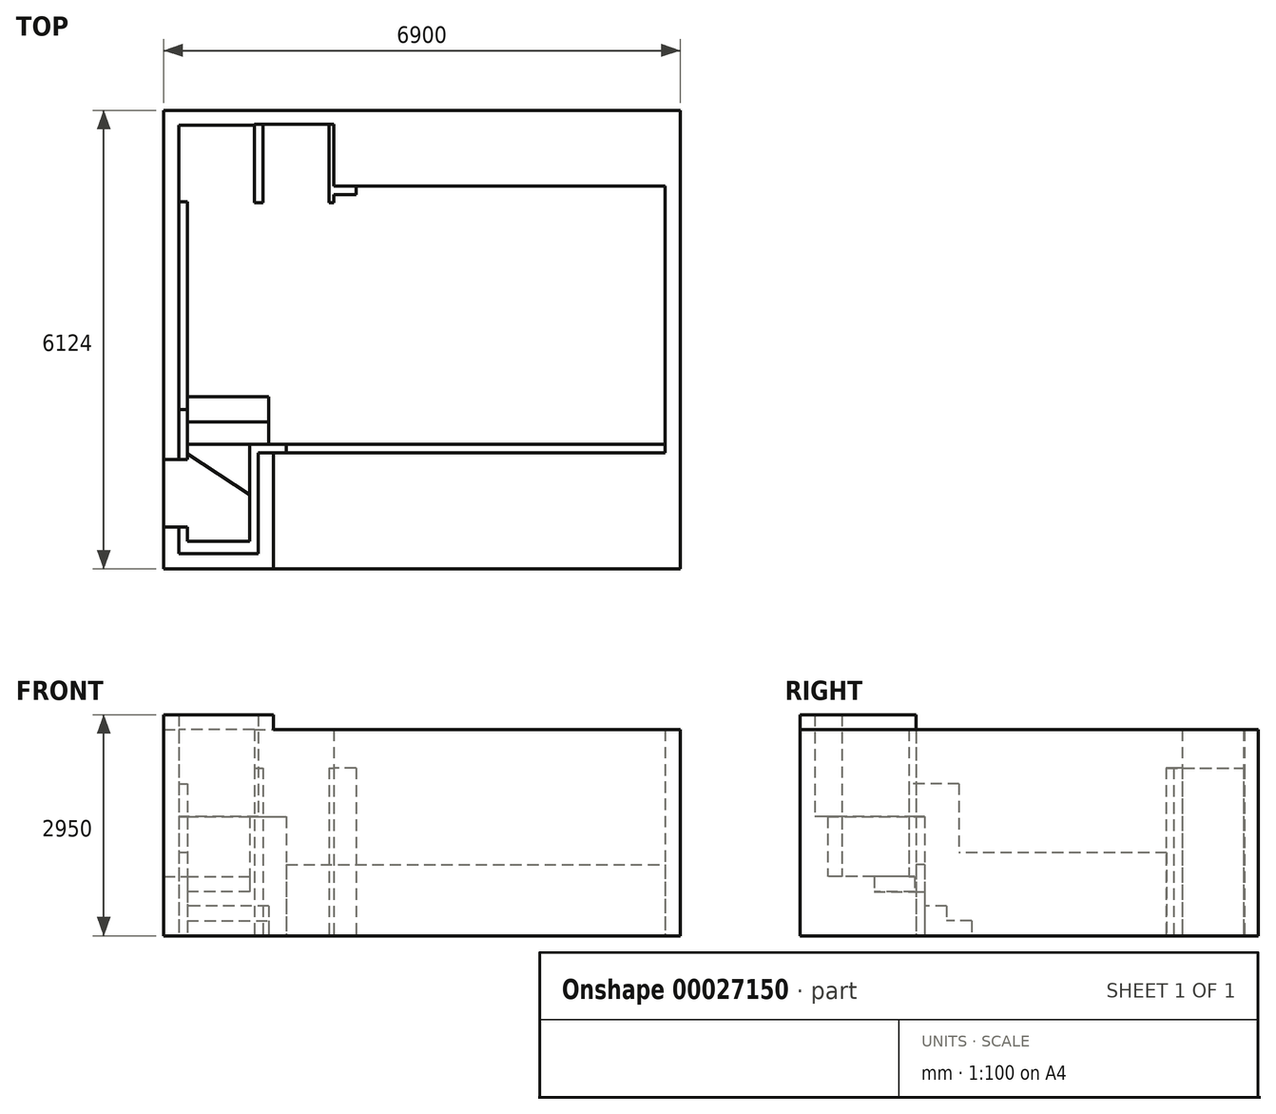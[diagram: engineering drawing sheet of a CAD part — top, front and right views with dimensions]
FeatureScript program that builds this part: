
annotation { "Feature Type Name" : "Feature", "Feature Type Description" : "" }
export const myFeature = defineFeature(function(context is Context, id is Id, definition is map)
    precondition{}
    {
        {
            var Q0;
            Q0=qCreatedBy(makeId("Top.planeOp"),FACE);
            var sketch = newSketch(context, id + "F0", { "sketchPlane" : qUnion([Q0])});
            skLineSegment(sketch, "E0", {"start": v(0, 0) * mm, "end": v(5550, 0) * mm});
            skLineSegment(sketch, "E1", {"start": v(5550, 0) * mm, "end": v(5550, 3560) * mm});
            skLineSegment(sketch, "E2", {"start": v(5550, 3560) * mm, "end": v(1060, 3560) * mm});
            skLineSegment(sketch, "E3", {"start": v(1060, 3342) * mm, "end": v(1060, 3560) * mm});
            skLineSegment(sketch, "E4", {"start": v(1060, 3342) * mm, "end": v(60, 3342) * mm});
            skLineSegment(sketch, "E5", {"start": v(0, 0) * mm, "end": v(0, -1350) * mm});
            skLineSegment(sketch, "E6", {"start": v(60, 3342) * mm, "end": v(60, 4374) * mm});
            skLineSegment(sketch, "E7", {"start": v(60, 4374) * mm, "end": v(-950, 4374) * mm});
            skLineSegment(sketch, "E8", {"start": v(-950, 4374) * mm, "end": v(-950, 3349) * mm});
            skLineSegment(sketch, "E9", {"start": v(-950, 3349) * mm, "end": v(-950, -91) * mm});
            skLineSegment(sketch, "E10", {"start": v(0, 115) * mm, "end": v(490, 115) * mm});
            skLineSegment(sketch, "E11", {"start": v(490, 115) * mm, "end": v(5550, 115) * mm});
            skLineSegment(sketch, "E12", {"start": v(0, 0) * mm, "end": v(0, 115) * mm});
            skLineSegment(sketch, "E13", {"start": v(5435, 0) * mm, "end": v(5435, 3560) * mm});
            skLineSegment(sketch, "E14", {"start": v(5435, 115) * mm, "end": v(5550, 115) * mm});
            skLineSegment(sketch, "E15", {"start": v(1060, 3445) * mm, "end": v(5550, 3445) * mm});
            skLineSegment(sketch, "E16", {"start": v(5435, 3445) * mm, "end": v(5435, 3560) * mm});
            skPoint(sketch, "E17", {"position": v(1420, 3560) * mm});
            skPoint(sketch, "E18", {"position": v(1120, 3560) * mm});
            skLineSegment(sketch, "E19", {"start": v(1120, 3560) * mm, "end": v(1120, 3342) * mm});
            skLineSegment(sketch, "E20", {"start": v(1120, 3342) * mm, "end": v(1060, 3342) * mm});
            skLineSegment(sketch, "E21", {"start": v(1420, 3560) * mm, "end": v(1420, 3445) * mm});
            skLineSegment(sketch, "E22", {"start": v(175, 3342) * mm, "end": v(175, 4374) * mm});
            skLineSegment(sketch, "E23", {"start": v(175, 4374) * mm, "end": v(60, 4374) * mm});
            skLineSegment(sketch, "E24", {"start": v(-950, -91) * mm, "end": v(-835, -91) * mm});
            skLineSegment(sketch, "E25", {"start": v(-835, -91) * mm, "end": v(-835, 3349) * mm});
            skLineSegment(sketch, "E26", {"start": v(-835, 3349) * mm, "end": v(-950, 3349) * mm});
            skLineSegment(sketch, "E27", {"start": v(-835, 745) * mm, "end": v(255, 745) * mm});
            skLineSegment(sketch, "E28", {"start": v(255, 745) * mm, "end": v(255, 115) * mm});
            skLineSegment(sketch, "E29", {"start": v(-835, 410) * mm, "end": v(255, 410) * mm});
            skLineSegment(sketch, "E30", {"start": v(0, 115) * mm, "end": v(-835, 115) * mm});
            skPoint(sketch, "E31", {"position": v(-835, -15) * mm});
            skPoint(sketch, "E32", {"position": v(0, -560) * mm});
            skLineSegment(sketch, "E33", {"start": v(-835, -15) * mm, "end": v(0, -560) * mm});
            skLineSegment(sketch, "E34", {"start": v(-835, -91) * mm, "end": v(-835, -991) * mm, "construction": true});
            skLineSegment(sketch, "E35", {"start": v(-835, -991) * mm, "end": v(-835, -1181) * mm});
            skLineSegment(sketch, "E36", {"start": v(-950, -991) * mm, "end": v(-835, -991) * mm});
            skLineSegment(sketch, "E37", {"start": v(-950, -991) * mm, "end": v(-950, -1350) * mm});
            skLineSegment(sketch, "E38", {"start": v(-950, -1350) * mm, "end": v(0, -1350) * mm});
            skLineSegment(sketch, "E39", {"start": v(-835, -1181) * mm, "end": v(0, -1181) * mm});
            skLineSegment(sketch, "E40", {"start": v(115, 115) * mm, "end": v(115, -1350) * mm});
            skLineSegment(sketch, "E41", {"start": v(115, -1350) * mm, "end": v(0, -1350) * mm});
            skPoint(sketch, "E42", {"position": v(130, 3342) * mm});
            skPoint(sketch, "E43", {"position": v(1000, 3342) * mm});
            skPoint(sketch, "E44", {"position": v(175, 3447) * mm});
            skPoint(sketch, "E45", {"position": v(175, 4387) * mm});
            skLineSegment(sketch, "E46", {"start": v(175, 4387) * mm, "end": v(175, 4374) * mm});
            skLineSegment(sketch, "E47", {"start": v(175, 4387) * mm, "end": v(1060, 4387) * mm});
            skLineSegment(sketch, "E48", {"start": v(1060, 4387) * mm, "end": v(1060, 3560) * mm});
            skLineSegment(sketch, "E49.bottom", {"start": v(-1150, 4574) * mm, "end": v(5750, 4574) * mm});
            skLineSegment(sketch, "E49.top", {"start": v(-1150, -1550) * mm, "end": v(5750, -1550) * mm});
            skLineSegment(sketch, "E49.left", {"start": v(-1150, 4574) * mm, "end": v(-1150, -1550) * mm});
            skLineSegment(sketch, "E49.right", {"start": v(5750, 4574) * mm, "end": v(5750, -1550) * mm});
            skLineSegment(sketch, "E50", {"start": v(-2093.54, -91) * mm, "end": v(-950, -91) * mm});
            skLineSegment(sketch, "E51", {"start": v(-2093.54, -991) * mm, "end": v(-950, -991) * mm});
            skLineSegment(sketch, "E52", {"start": v(315, 0) * mm, "end": v(315, -1550) * mm});
            skLineSegment(sketch, "E53", {"start": v(490, 115) * mm, "end": v(490, 0) * mm});
            skLineSegment(sketch, "E54", {"start": v(1120, 3560) * mm, "end": v(1120, 4574) * mm});
            skLineSegment(sketch, "E55", {"start": v(60, 4374) * mm, "end": v(60, 4574) * mm});
            skLineSegment(sketch, "E56", {"start": v(1060, 4387) * mm, "end": v(1120, 4387) * mm});
            skPoint(sketch, "E57", {"position": v(-950, 575) * mm});
            skLineSegment(sketch, "E58", {"start": v(-950, 575) * mm, "end": v(-835, 575) * mm});
            skSolve(sketch);
        }
        {
            var Q0;
            {var subQ1=sQuery(id+"F0.wireOp",EDGE,"E49.right");Q0=makeQuery(id+"F0.imprint","IMPRINT",FACE,{"disambiguationData":[TD([[makeQuery(id+"F0.imprint","IMPRINT",EDGE,{"derivedFrom":subQ1}),-1.0]])]});}
            extrude(context, id + "F1", {"entities" : qUnion([Q0]), "depth" : 2750 * mm});
        }
        {
            var Q0;
            {var subQ4=sQuery(id+"F0.wireOp",EDGE,"E37");Q0=makeQuery(id+"F0.imprint","IMPRINT",FACE,{"disambiguationData":[TD([[makeQuery(id+"F0.imprint","IMPRINT",EDGE,{"derivedFrom":subQ4}),-1.0]])]});}
            extrude(context, id + "F2", {"entities" : qUnion([Q0]), "operationType" : NewBodyOperationType.ADD, "depth" : 2950 * mm});
        }
        {
            var Q0;
            {var subQ0=sQuery(id+"F0.wireOp",EDGE,"E53");Q0=makeQuery(id+"F0.imprint","IMPRINT",FACE,{"disambiguationData":[TD([[makeQuery(id+"F0.imprint","IMPRINT",EDGE,{"derivedFrom":subQ0}),-1.0]])]});}
            var Q1;
            {var subQ5=sQuery(id+"F0.wireOp",EDGE,"E12");Q1=makeQuery(id+"F0.imprint","IMPRINT",FACE,{"disambiguationData":[TD([[makeQuery(id+"F0.imprint","IMPRINT",EDGE,{"derivedFrom":subQ5}),-1.0]])]});}
            var Q2;
            {var subQ0=sQuery(id+"F0.wireOp",EDGE,"E41");Q2=makeQuery(id+"F0.imprint","IMPRINT",FACE,{"disambiguationData":[TD([[makeQuery(id+"F0.imprint","IMPRINT",EDGE,{"derivedFrom":subQ0}),-1.0]])]});}
            var Q3;
            Q3=makeQuery(id+"F0.imprint","IMPRINT",FACE,{"disambiguationData":[TD([[makeQuery(id+"F0.imprint","IMPRINT",EDGE,{"derivedFrom":sQuery(id+"F0.wireOp",EDGE,"E35")}),-1.0]])]});
            extrude(context, id + "F3", {"entities" : qUnion([Q0, Q1, Q2, Q3]), "depth" : 1590 * mm});
        }
        {
            var Q0;
            {var subQ4=sQuery(id+"F0.wireOp",EDGE,"E11");Q0=makeQuery(id+"F0.imprint","IMPRINT",FACE,{"disambiguationData":[TD([[makeQuery(id+"F0.imprint","IMPRINT",EDGE,{"derivedFrom":subQ4}),-1.0]])]});}
            var Q1;
            {var subQ5=sQuery(id+"F0.wireOp",EDGE,"E14");Q1=makeQuery(id+"F0.imprint","IMPRINT",FACE,{"disambiguationData":[TD([[makeQuery(id+"F0.imprint","IMPRINT",EDGE,{"derivedFrom":subQ5}),1.0]])]});}
            var Q2;
            {var subQ0=sQuery(id+"F0.wireOp",EDGE,"E14");Q2=makeQuery(id+"F0.imprint","IMPRINT",FACE,{"disambiguationData":[TD([[makeQuery(id+"F0.imprint","IMPRINT",EDGE,{"derivedFrom":subQ0}),-1.0]])]});}
            var Q3;
            {var subQ0=sQuery(id+"F0.wireOp",EDGE,"E16");Q3=makeQuery(id+"F0.imprint","IMPRINT",FACE,{"disambiguationData":[TD([[makeQuery(id+"F0.imprint","IMPRINT",EDGE,{"derivedFrom":subQ0}),-1.0]])]});}
            var Q4;
            {var subQ1=sQuery(id+"F0.wireOp",EDGE,"E16");Q4=makeQuery(id+"F0.imprint","IMPRINT",FACE,{"disambiguationData":[TD([[makeQuery(id+"F0.imprint","IMPRINT",EDGE,{"derivedFrom":subQ1}),1.0]])]});}
            extrude(context, id + "F4", {"entities" : qUnion([Q0, Q1, Q2, Q3, Q4]), "depth" : 950 * mm});
        }
        {
            var Q0;
            {var subQ1=sQuery(id+"F0.wireOp",EDGE,"E6");Q0=makeQuery(id+"F0.imprint","IMPRINT",FACE,{"disambiguationData":[TD([[makeQuery(id+"F0.imprint","IMPRINT",EDGE,{"derivedFrom":subQ1}),-1.0]])]});}
            var Q1;
            {var subQ0=sQuery(id+"F0.wireOp",EDGE,"E20");Q1=makeQuery(id+"F0.imprint","IMPRINT",FACE,{"disambiguationData":[TD([[makeQuery(id+"F0.imprint","IMPRINT",EDGE,{"derivedFrom":subQ0}),-1.0]])]});}
            var Q2;
            {var subQ1=sQuery(id+"F0.wireOp",EDGE,"E15");var subQ5=sQuery(id+"F0.wireOp",EDGE,"E3");var subQ6=makeQuery(id+"F0.imprint","INTERSECT",VERTEX,{"derivedFrom":[subQ5,subQ1]});Q2=makeQuery(id+"F0.imprint","IMPRINT",FACE,{"disambiguationData":[TD([[makeQuery(id+"F0.imprint","IMPRINT",EDGE,{"disambiguationData":[TD([[subQ6,-1.0]])],"derivedFrom":subQ1}),1.0]])]});}
            var Q3;
            {var subQ0=sQuery(id+"F0.wireOp",EDGE,"E21");Q3=makeQuery(id+"F0.imprint","IMPRINT",FACE,{"disambiguationData":[TD([[makeQuery(id+"F0.imprint","IMPRINT",EDGE,{"derivedFrom":subQ0}),-1.0]])]});}
            var Q4;
            Q4=makeQuery(id+"F0.imprint","IMPRINT",FACE,{"disambiguationData":[TD([[makeQuery(id+"F0.imprint","IMPRINT",EDGE,{"derivedFrom":sQuery(id+"F0.wireOp",EDGE,"E23")}),-1.0]])]});
            var Q5;
            {var subQ4=sQuery(id+"F0.wireOp",EDGE,"E48");Q5=makeQuery(id+"F0.imprint","IMPRINT",FACE,{"disambiguationData":[TD([[makeQuery(id+"F0.imprint","IMPRINT",EDGE,{"derivedFrom":subQ4}),1.0]])]});}
            extrude(context, id + "F5", {"entities" : qUnion([Q0, Q1, Q2, Q3, Q4, Q5]), "depth" : 2240 * mm});
        }
        {
            var Q0;
            {var subQ6=sQuery(id+"F0.wireOp",EDGE,"E24");Q0=makeQuery(id+"F0.imprint","IMPRINT",FACE,{"disambiguationData":[TD([[makeQuery(id+"F0.imprint","IMPRINT",EDGE,{"derivedFrom":subQ6}),-1.0]])]});}
            extrude(context, id + "F6", {"entities" : qUnion([Q0]), "operationType" : NewBodyOperationType.ADD, "depth" : 790 * mm});
        }
        {
            var Q0;
            Q0=makeQuery(id+"F5.opExtrude","CAP_FACE",FACE,{"disambiguationData":[OSD([sQuery(id+"F0.wireOp",EDGE,"E2"),sQuery(id+"F0.wireOp",EDGE,"E3"),sQuery(id+"F0.wireOp",EDGE,"E4"),sQuery(id+"F0.wireOp",EDGE,"E6"),sQuery(id+"F0.wireOp",EDGE,"E15"),sQuery(id+"F0.wireOp",EDGE,"E19"),sQuery(id+"F0.wireOp",EDGE,"E20"),sQuery(id+"F0.wireOp",EDGE,"E21"),sQuery(id+"F0.wireOp",EDGE,"E22"),sQuery(id+"F0.wireOp",EDGE,"E46"),sQuery(id+"F0.wireOp",EDGE,"E47"),sQuery(id+"F0.wireOp",EDGE,"E48"),sQuery(id+"F0.wireOp",EDGE,"E49.bottom"),sQuery(id+"F0.wireOp",EDGE,"E54"),sQuery(id+"F0.wireOp",EDGE,"E55")])],"isStart":false});
            var sketch = newSketch(context, id + "F7", { "sketchPlane" : qUnion([Q0])});
            skLineSegment(sketch, "E59.bottom", {"start": v(60, 4574) * mm, "end": v(1120, 4574) * mm});
            skLineSegment(sketch, "E59.top", {"start": v(60, 4387) * mm, "end": v(1120, 4387) * mm});
            skLineSegment(sketch, "E59.left", {"start": v(60, 4574) * mm, "end": v(60, 4387) * mm});
            skLineSegment(sketch, "E59.right", {"start": v(1120, 4574) * mm, "end": v(1120, 4387) * mm});
            skSolve(sketch);
        }
        {
            var Q0;
            Q0=qSketchRegion(id+"F7",true);
            var Q1;
            Q1=makeQuery(id+"F1.opExtrude","CAP_FACE",FACE,{"disambiguationData":[OSD([sQuery(id+"F0.wireOp",EDGE,"E0"),sQuery(id+"F0.wireOp",EDGE,"E1"),sQuery(id+"F0.wireOp",EDGE,"E2"),sQuery(id+"F0.wireOp",EDGE,"E49.bottom"),sQuery(id+"F0.wireOp",EDGE,"E49.top"),sQuery(id+"F0.wireOp",EDGE,"E49.right"),sQuery(id+"F0.wireOp",EDGE,"E52"),sQuery(id+"F0.wireOp",EDGE,"E54")])],"isStart":false});
            extrude(context, id + "F8", {"entities" : qUnion([Q0]), "operationType" : NewBodyOperationType.ADD, "endBound" : BoundingType.UP_TO_SURFACE, "endBoundEntityFace" : qUnion([Q1]), "depth" : 25 * mm});
        }
        {
            var Q0;
            Q0=makeQuery(id+"F0.imprint","IMPRINT",FACE,{"disambiguationData":[TD([[makeQuery(id+"F0.imprint","IMPRINT",EDGE,{"derivedFrom":sQuery(id+"F0.wireOp",EDGE,"E7")}),-1.0]])]});
            var Q1;
            Q1=makeQuery(id+"F8.boolean.opBoolean","MERGE",FACE,{"derivedFrom":[makeQuery(id+"F1.opExtrude","CAP_FACE",FACE,{"disambiguationData":[OSD([sQuery(id+"F0.wireOp",EDGE,"E0"),sQuery(id+"F0.wireOp",EDGE,"E1"),sQuery(id+"F0.wireOp",EDGE,"E2"),sQuery(id+"F0.wireOp",EDGE,"E49.bottom"),sQuery(id+"F0.wireOp",EDGE,"E49.top"),sQuery(id+"F0.wireOp",EDGE,"E49.right"),sQuery(id+"F0.wireOp",EDGE,"E52"),sQuery(id+"F0.wireOp",EDGE,"E54")])],"isStart":false}),makeQuery(id+"F8.opExtrude","CAP_FACE",FACE,{"disambiguationData":[OSD([sQuery(id+"F7.wireOp",EDGE,"E59.bottom"),sQuery(id+"F7.wireOp",EDGE,"E59.top"),sQuery(id+"F7.wireOp",EDGE,"E59.left"),sQuery(id+"F7.wireOp",EDGE,"E59.right")])],"isStart":false})]});
            extrude(context, id + "F9", {"entities" : qUnion([Q0]), "operationType" : NewBodyOperationType.ADD, "endBound" : BoundingType.UP_TO_SURFACE, "endBoundEntityFace" : qUnion([Q1]), "depth" : 25 * mm});
        }
        {
            var Q0;
            {var subQ3=sQuery(id+"F0.wireOp",EDGE,"E12");Q0=makeQuery(id+"F0.imprint","IMPRINT",FACE,{"disambiguationData":[TD([[makeQuery(id+"F0.imprint","IMPRINT",EDGE,{"derivedFrom":subQ3}),1.0]])]});}
            extrude(context, id + "F10", {"entities" : qUnion([Q0]), "operationType" : NewBodyOperationType.ADD, "depth" : 590 * mm});
        }
        {
            var Q0;
            {var subQ1=sQuery(id+"F0.wireOp",EDGE,"E29");Q0=makeQuery(id+"F0.imprint","IMPRINT",FACE,{"disambiguationData":[TD([[makeQuery(id+"F0.imprint","IMPRINT",EDGE,{"derivedFrom":subQ1}),-1.0]])]});}
            extrude(context, id + "F11", {"entities" : qUnion([Q0]), "operationType" : NewBodyOperationType.ADD, "depth" : 400 * mm});
        }
        {
            var Q0;
            Q0=makeQuery(id+"F0.imprint","IMPRINT",FACE,{"disambiguationData":[TD([[makeQuery(id+"F0.imprint","IMPRINT",EDGE,{"derivedFrom":sQuery(id+"F0.wireOp",EDGE,"E9")}),1.0]])]});
            extrude(context, id + "F12", {"entities" : qUnion([Q0]), "depth" : 1110 * mm});
        }
        {
            var Q0;
            {var subQ5=sQuery(id+"F0.wireOp",EDGE,"E24");Q0=makeQuery(id+"F0.imprint","IMPRINT",FACE,{"disambiguationData":[TD([[makeQuery(id+"F0.imprint","IMPRINT",EDGE,{"derivedFrom":subQ5}),1.0]])]});}
            extrude(context, id + "F13", {"entities" : qUnion([Q0]), "operationType" : NewBodyOperationType.ADD, "depth" : 2030 * mm});
        }
        {
            var Q0;
            {var subQ2=sQuery(id+"F0.wireOp",EDGE,"E27");Q0=makeQuery(id+"F0.imprint","IMPRINT",FACE,{"disambiguationData":[TD([[makeQuery(id+"F0.imprint","IMPRINT",EDGE,{"derivedFrom":subQ2}),-1.0]])]});}
            extrude(context, id + "F14", {"entities" : qUnion([Q0]), "operationType" : NewBodyOperationType.ADD, "depth" : 200 * mm});
        }
    });
